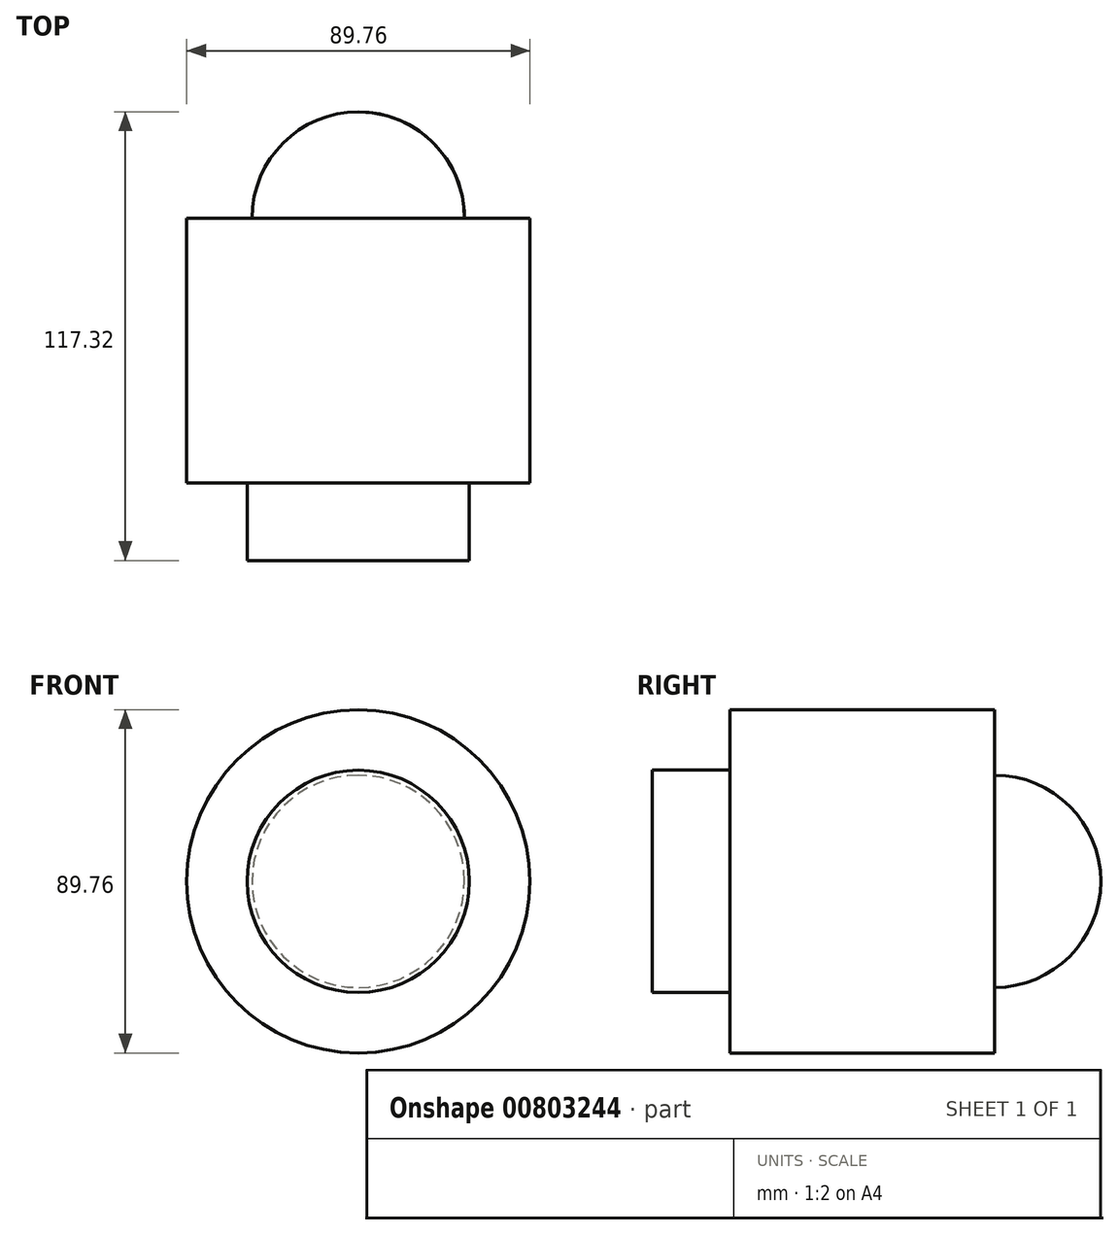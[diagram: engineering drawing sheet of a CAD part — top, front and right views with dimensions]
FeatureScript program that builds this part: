
annotation { "Feature Type Name" : "Feature", "Feature Type Description" : "" }
export const myFeature = defineFeature(function(context is Context, id is Id, definition is map)
    precondition{}
    {
        {
            var Q0;
            Q0=qCreatedBy(makeId("Top.planeOp"),FACE);
            var sketch = newSketch(context, id + "F0", { "sketchPlane" : qUnion([Q0])});
            skLineSegment(sketch, "E0", {"start": v(0, 74.99) * mm, "end": v(0, -76.14) * mm, "construction": true});
            skLineSegment(sketch, "E1.bottom", {"start": v(27.75, 38.31) * mm, "end": v(44.88, 38.31) * mm});
            skLineSegment(sketch, "E1.top", {"start": v(29.05, -30.98) * mm, "end": v(44.88, -30.98) * mm});
            skLineSegment(sketch, "E1.left", {"start": v(0, 38.31) * mm, "end": v(0, -30.98) * mm, "construction": true});
            skLineSegment(sketch, "E1.right", {"start": v(44.88, 38.31) * mm, "end": v(44.88, -30.98) * mm});
            skLineSegment(sketch, "E2.top", {"start": v(0, -51.25) * mm, "end": v(29.05, -51.25) * mm});
            skLineSegment(sketch, "E2.right", {"start": v(29.05, -30.98) * mm, "end": v(29.05, -51.25) * mm});
            skArc(sketch, "E3", {"start": v(27.75, 38.31) * mm, "mid": v(19.62, 57.94) * mm, "end": v(0, 66.07) * mm});
            skPoint(sketch, "E4.orphan", {"position": v(-26.35, 0) * mm});
            skLineSegment(sketch, "E5", {"start": v(0, 66.07) * mm, "end": v(0, -51.25) * mm});
            skSolve(sketch);
        }
        {
            var Q0;
            Q0=makeQuery(id+"F0.imprint","IMPRINT",FACE,{"disambiguationData":[TD([[makeQuery(id+"F0.imprint","IMPRINT",EDGE,{"derivedFrom":sQuery(id+"F0.wireOp",EDGE,"E1.bottom")}),-1.0]])]});
            var Q1;
            Q1=sQuery(id+"F0.wireOp",EDGE,"E0");
            revolve(context, id + "F1", {"surfaceOperationType" : NewSurfaceOperationType.NEW, "entities" : qUnion([Q0]), "axis" : qUnion([Q1]), "revolveType" : RevolveType.FULL});
        }
    });
